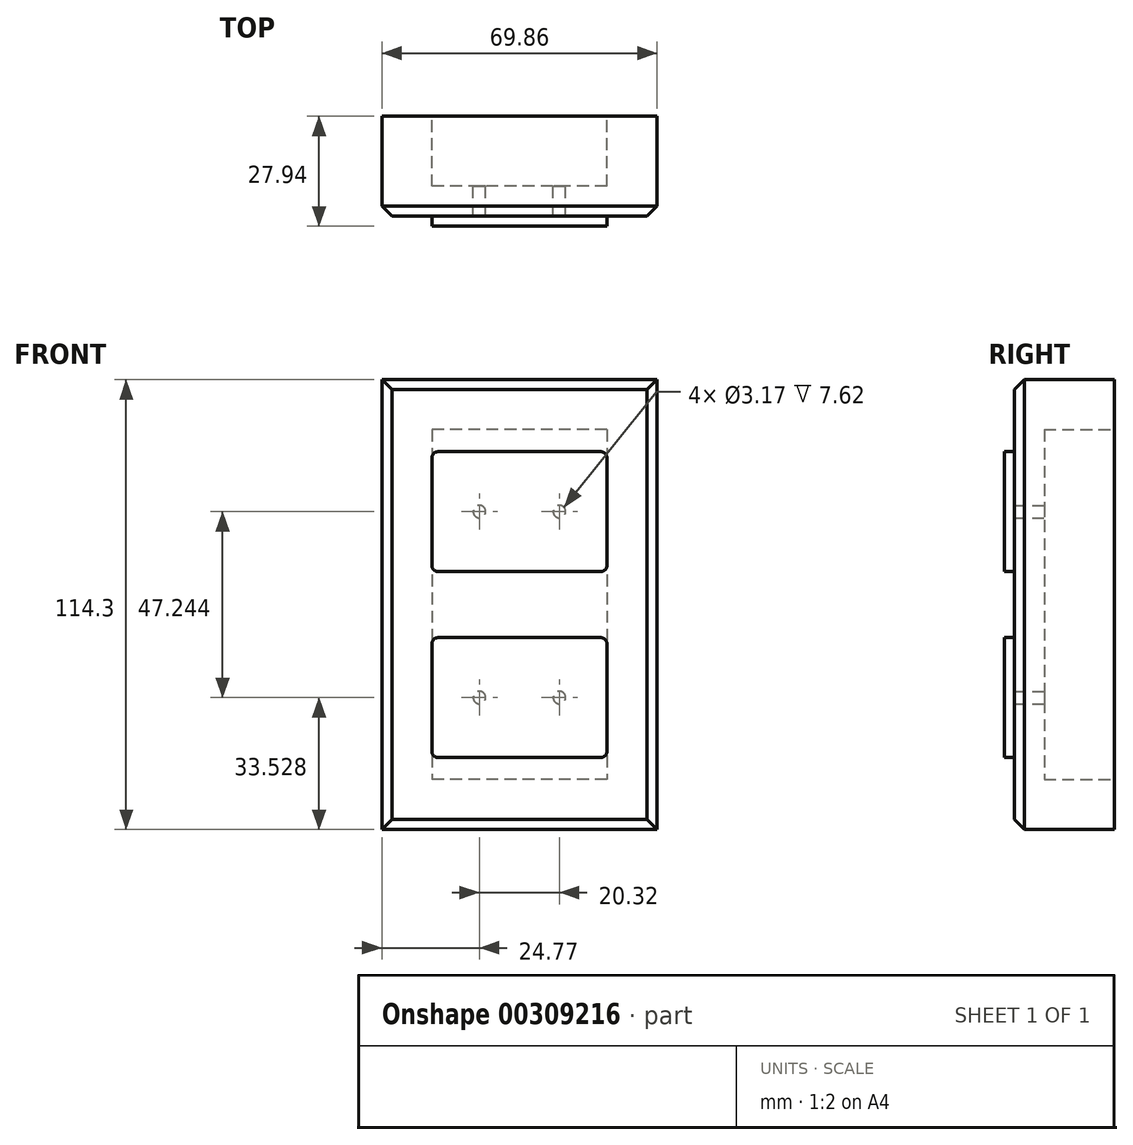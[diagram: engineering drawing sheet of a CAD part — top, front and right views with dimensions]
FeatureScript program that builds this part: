
annotation { "Feature Type Name" : "Feature", "Feature Type Description" : "" }
export const myFeature = defineFeature(function(context is Context, id is Id, definition is map)
    precondition{}
    {
        {
            var Q0;
            Q0=qCreatedBy(makeId("Front.planeOp"),FACE);
            var sketch = newSketch(context, id + "F0", { "sketchPlane" : qUnion([Q0])});
            skLineSegment(sketch, "E0.bottom", {"start": v(34.93, 57.15) * mm, "end": v(-34.92, 57.15) * mm});
            skLineSegment(sketch, "E0.top", {"start": v(34.92, -57.15) * mm, "end": v(-34.92, -57.15) * mm});
            skLineSegment(sketch, "E0.left", {"start": v(34.93, 57.15) * mm, "end": v(34.93, -57.15) * mm});
            skLineSegment(sketch, "E0.right", {"start": v(-34.93, 57.15) * mm, "end": v(-34.93, -57.15) * mm});
            skPoint(sketch, "E0.middle", {"position": v(0, 0) * mm});
            skLineSegment(sketch, "E1", {"start": v(0, 57.15) * mm, "end": v(0, -57.15) * mm, "construction": true});
            skSolve(sketch);
        }
        {
            var Q0;
            Q0 = qSketchRegion(id + "F0", true);
            extrude(context, id + "F1", {"entities" : qUnion([Q0]), "depth" : 25.4 * mm});
        }
        {
            var Q0;
            Q0=makeQuery(id+"F1.opExtrude","CAP_EDGE",EDGE,{"disambiguationData":[OSD([sQuery(id+"F0.wireOp",EDGE,"E0.right")])],"isStart":false});
            var Q1;
            Q1=makeQuery(id+"F1.opExtrude","CAP_EDGE",EDGE,{"disambiguationData":[OSD([sQuery(id+"F0.wireOp",EDGE,"E0.bottom")])],"isStart":false});
            var Q2;
            Q2=makeQuery(id+"F1.opExtrude","CAP_EDGE",EDGE,{"disambiguationData":[OSD([sQuery(id+"F0.wireOp",EDGE,"E0.left")])],"isStart":false});
            var Q3;
            Q3=makeQuery(id+"F1.opExtrude","CAP_EDGE",EDGE,{"disambiguationData":[OSD([sQuery(id+"F0.wireOp",EDGE,"E0.top")])],"isStart":false});
            chamfer(context, id + "F2", {"entities" : qUnion([Q0, Q1, Q2, Q3]), "width" : 2.54 * mm, "tangentPropagation" : true});
        }
        {
            var Q0;
            Q0=makeQuery(id+"F1.opExtrude","CAP_FACE",FACE,{"disambiguationData":[OSD([sQuery(id+"F0.wireOp",EDGE,"E0.bottom"),sQuery(id+"F0.wireOp",EDGE,"E0.top"),sQuery(id+"F0.wireOp",EDGE,"E0.left"),sQuery(id+"F0.wireOp",EDGE,"E0.right")])],"isStart":false});
            var sketch = newSketch(context, id + "F3", { "sketchPlane" : qUnion([Q0])});
            skLineSegment(sketch, "E2.bottom", {"start": v(-20.64, 38.86) * mm, "end": v(20.64, 38.86) * mm});
            skLineSegment(sketch, "E2.top", {"start": v(-20.64, 8.38) * mm, "end": v(20.64, 8.38) * mm});
            skLineSegment(sketch, "E2.left", {"start": v(-22.23, 37.27) * mm, "end": v(-22.23, 9.97) * mm});
            skLineSegment(sketch, "E2.right", {"start": v(22.23, 37.27) * mm, "end": v(22.23, 9.97) * mm});
            skPoint(sketch, "E2.middle", {"position": v(0, 23.62) * mm});
            skLineSegment(sketch, "E3.bottom", {"start": v(-20.64, -8.38) * mm, "end": v(20.64, -8.38) * mm});
            skLineSegment(sketch, "E3.top", {"start": v(-20.64, -38.86) * mm, "end": v(20.64, -38.86) * mm});
            skLineSegment(sketch, "E3.left", {"start": v(-22.23, -9.97) * mm, "end": v(-22.23, -37.27) * mm});
            skLineSegment(sketch, "E3.right", {"start": v(22.23, -9.97) * mm, "end": v(22.23, -37.27) * mm});
            skPoint(sketch, "E3.middle", {"position": v(0, -23.62) * mm});
            skPoint(sketch, "E4.visualSharp", {"position": v(-22.23, 38.86) * mm});
            skArc(sketch, "E4.filletArc", {"start": v(-20.64, 38.86) * mm, "mid": v(-21.76, 38.4) * mm, "end": v(-22.23, 37.27) * mm});
            skPoint(sketch, "E5.visualSharp", {"position": v(22.23, 38.86) * mm});
            skArc(sketch, "E5.filletArc", {"start": v(22.22, 37.27) * mm, "mid": v(21.76, 38.4) * mm, "end": v(20.64, 38.86) * mm});
            skPoint(sketch, "E6.visualSharp", {"position": v(22.23, 8.38) * mm});
            skArc(sketch, "E6.filletArc", {"start": v(20.64, 8.38) * mm, "mid": v(21.76, 8.85) * mm, "end": v(22.23, 9.97) * mm});
            skPoint(sketch, "E7.visualSharp", {"position": v(-22.23, 8.38) * mm});
            skArc(sketch, "E7.filletArc", {"start": v(-22.23, 9.97) * mm, "mid": v(-21.76, 8.85) * mm, "end": v(-20.64, 8.38) * mm});
            skPoint(sketch, "E8.visualSharp", {"position": v(22.23, -38.86) * mm});
            skArc(sketch, "E8.filletArc", {"start": v(20.64, -38.86) * mm, "mid": v(21.76, -38.4) * mm, "end": v(22.22, -37.27) * mm});
            skPoint(sketch, "E9.visualSharp", {"position": v(22.23, -8.38) * mm});
            skArc(sketch, "E9.filletArc", {"start": v(22.23, -9.97) * mm, "mid": v(21.76, -8.85) * mm, "end": v(20.64, -8.38) * mm});
            skPoint(sketch, "E10.visualSharp", {"position": v(-22.23, -8.38) * mm});
            skArc(sketch, "E10.filletArc", {"start": v(-20.64, -8.38) * mm, "mid": v(-21.76, -8.85) * mm, "end": v(-22.23, -9.97) * mm});
            skPoint(sketch, "E11.visualSharp", {"position": v(-22.23, -38.86) * mm});
            skArc(sketch, "E11.filletArc", {"start": v(-22.22, -37.27) * mm, "mid": v(-21.76, -38.4) * mm, "end": v(-20.64, -38.86) * mm});
            skSolve(sketch);
        }
        {
            var Q0;
            Q0 = qSketchRegion(id + "F3", true);
            extrude(context, id + "F4", {"entities" : qUnion([Q0]), "operationType" : NewBodyOperationType.REMOVE, "oppositeDirection" : true, "depth" : 2.54 * mm});
        }
        {
            var Q0;
            Q0=makeQuery(id+"F3.imprint","IMPRINT",FACE,{"disambiguationData":[TD([[makeQuery(id+"F3.imprint","IMPRINT",EDGE,{"derivedFrom":sQuery(id+"F3.wireOp",EDGE,"E2.bottom")}),-1.0]])]});
            var Q1;
            Q1=makeQuery(id+"F3.imprint","IMPRINT",FACE,{"disambiguationData":[TD([[makeQuery(id+"F3.imprint","IMPRINT",EDGE,{"derivedFrom":sQuery(id+"F3.wireOp",EDGE,"E3.bottom")}),-1.0]])]});
            extrude(context, id + "F5", {"entities" : qUnion([Q0, Q1]), "depth" : 2.54 * mm});
        }
        {
            var Q0;
            Q0=makeQuery(id+"F3.imprint","IMPRINT",FACE,{"disambiguationData":[TD([[makeQuery(id+"F3.imprint","IMPRINT",EDGE,{"derivedFrom":sQuery(id+"F3.wireOp",EDGE,"E2.bottom")}),-1.0]])]});
            extrude(context, id + "F6", {"entities" : qUnion([Q0]), "operationType" : NewBodyOperationType.ADD, "oppositeDirection" : true, "depth" : 2.54 * mm});
        }
        {
            var Q0;
            Q0=makeQuery(id+"F3.imprint","IMPRINT",FACE,{"disambiguationData":[TD([[makeQuery(id+"F3.imprint","IMPRINT",EDGE,{"derivedFrom":sQuery(id+"F3.wireOp",EDGE,"E3.bottom")}),-1.0]])]});
            extrude(context, id + "F7", {"entities" : qUnion([Q0]), "operationType" : NewBodyOperationType.ADD, "oppositeDirection" : true, "depth" : 2.54 * mm});
        }
        {
            var Q0;
            Q0=makeQuery(id+"F1.opExtrude","CAP_FACE",FACE,{"disambiguationData":[OSD([sQuery(id+"F0.wireOp",EDGE,"E0.bottom"),sQuery(id+"F0.wireOp",EDGE,"E0.top"),sQuery(id+"F0.wireOp",EDGE,"E0.left"),sQuery(id+"F0.wireOp",EDGE,"E0.right")])],"isStart":true});
            var sketch = newSketch(context, id + "F8", { "sketchPlane" : qUnion([Q0])});
            skLineSegment(sketch, "E12.bottom", {"start": v(-22.23, 44.45) * mm, "end": v(22.23, 44.45) * mm});
            skLineSegment(sketch, "E12.top", {"start": v(-22.23, -44.45) * mm, "end": v(22.23, -44.45) * mm});
            skLineSegment(sketch, "E12.left", {"start": v(-22.23, 44.45) * mm, "end": v(-22.23, -44.45) * mm});
            skLineSegment(sketch, "E12.right", {"start": v(22.23, 44.45) * mm, "end": v(22.23, -44.45) * mm});
            skPoint(sketch, "E12.middle", {"position": v(0, 0) * mm});
            skSolve(sketch);
        }
        {
            var Q0;
            Q0 = qSketchRegion(id + "F8", true);
            extrude(context, id + "F9", {"entities" : qUnion([Q0]), "operationType" : NewBodyOperationType.REMOVE, "oppositeDirection" : true, "depth" : 17.78 * mm});
        }
        {
            var Q0;
            Q0=makeQuery(id+"F9.boolean.opBoolean","COPY",FACE,{"derivedFrom":makeQuery(id+"F9.opExtrude","CAP_FACE",FACE,{"disambiguationData":[OSD([sQuery(id+"F8.wireOp",EDGE,"E12.bottom"),sQuery(id+"F8.wireOp",EDGE,"E12.top"),sQuery(id+"F8.wireOp",EDGE,"E12.left"),sQuery(id+"F8.wireOp",EDGE,"E12.right")])],"isStart":false})});
            var sketch = newSketch(context, id + "F10", { "sketchPlane" : qUnion([Q0])});
            skLineSegment(sketch, "E13.bottom", {"start": v(10.16, 23.62) * mm, "end": v(-10.16, 23.62) * mm, "construction": true});
            skLineSegment(sketch, "E13.top", {"start": v(10.16, -23.62) * mm, "end": v(-10.16, -23.62) * mm, "construction": true});
            skLineSegment(sketch, "E13.left", {"start": v(10.16, 23.62) * mm, "end": v(10.16, -23.62) * mm, "construction": true});
            skLineSegment(sketch, "E13.right", {"start": v(-10.16, 23.62) * mm, "end": v(-10.16, -23.62) * mm, "construction": true});
            skPoint(sketch, "E13.middle", {"position": v(0, 0) * mm});
            skCircle(sketch, "E14", {"center": v(-10.16, 23.62) * mm, "radius": 1.59 * mm});
            skCircle(sketch, "E15", {"center": v(10.16, -23.62) * mm, "radius": 1.59 * mm});
            skCircle(sketch, "E16", {"center": v(-10.16, -23.62) * mm, "radius": 1.59 * mm});
            skCircle(sketch, "E17", {"center": v(10.16, 23.62) * mm, "radius": 1.59 * mm});
            skSolve(sketch);
        }
        {
            var Q0;
            Q0=makeQuery(id+"F10.imprint","IMPRINT",FACE,{"disambiguationData":[TD([[makeQuery(id+"F10.imprint","IMPRINT",EDGE,{"derivedFrom":sQuery(id+"F10.wireOp",EDGE,"E14")}),1.0]])]});
            var Q1;
            Q1=makeQuery(id+"F10.imprint","IMPRINT",FACE,{"disambiguationData":[TD([[makeQuery(id+"F10.imprint","IMPRINT",EDGE,{"derivedFrom":sQuery(id+"F10.wireOp",EDGE,"E17")}),1.0]])]});
            var Q2;
            Q2=makeQuery(id+"F10.imprint","IMPRINT",FACE,{"disambiguationData":[TD([[makeQuery(id+"F10.imprint","IMPRINT",EDGE,{"derivedFrom":sQuery(id+"F10.wireOp",EDGE,"E16")}),1.0]])]});
            var Q3;
            Q3=makeQuery(id+"F10.imprint","IMPRINT",FACE,{"disambiguationData":[TD([[makeQuery(id+"F10.imprint","IMPRINT",EDGE,{"derivedFrom":sQuery(id+"F10.wireOp",EDGE,"E15")}),1.0]])]});
            var Q4;
            Q4=sQuery(id+"F10.wireOp",EDGE,"E14");
            var Q5;
            Q5=sQuery(id+"F10.wireOp",EDGE,"E17");
            var Q6;
            Q6=sQuery(id+"F10.wireOp",EDGE,"E15");
            var Q7;
            Q7=sQuery(id+"F10.wireOp",EDGE,"E16");
            extrude(context, id + "F11", {"entities" : qUnion([Q0, Q1, Q2, Q3]), "operationType" : NewBodyOperationType.REMOVE, "surfaceEntities" : qUnion([Q4, Q5, Q6, Q7]), "oppositeDirection" : true, "depth" : 7.62 * mm});
        }
    });
